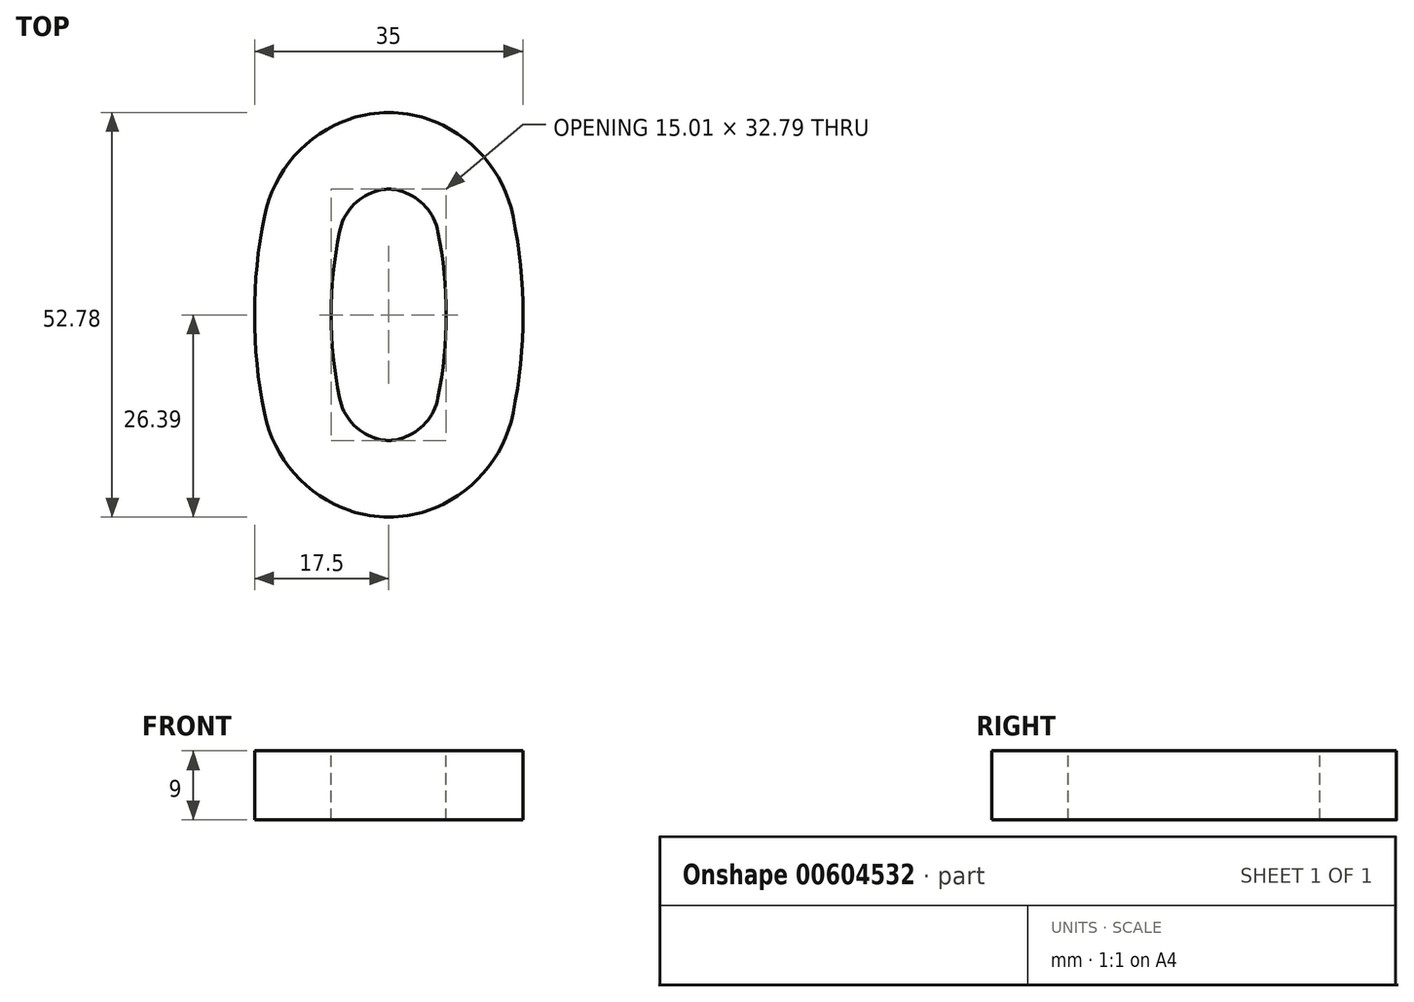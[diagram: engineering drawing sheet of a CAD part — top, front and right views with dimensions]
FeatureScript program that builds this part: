
annotation { "Feature Type Name" : "Feature", "Feature Type Description" : "" }
export const myFeature = defineFeature(function(context is Context, id is Id, definition is map)
    precondition{}
    {
        {
            var Q0;
            Q0=qCreatedBy(makeId("Top.planeOp"),FACE);
            var sketch = newSketch(context, id + "F0", { "sketchPlane" : qUnion([Q0])});
            skLineSegment(sketch, "E0.bottom", {"start": v(-15.38, -16.5) * mm, "end": v(15.38, -16.5) * mm, "construction": true});
            skLineSegment(sketch, "E0.top", {"start": v(-15.37, 16.5) * mm, "end": v(15.38, 16.5) * mm, "construction": true});
            skLineSegment(sketch, "E0.left", {"start": v(-15.38, -16.5) * mm, "end": v(-15.38, 16.5) * mm, "construction": true});
            skLineSegment(sketch, "E0.right", {"start": v(15.38, -16.5) * mm, "end": v(15.38, 16.5) * mm, "construction": true});
            skPoint(sketch, "E0.middle", {"position": v(0, 0) * mm});
            skLineSegment(sketch, "E1", {"start": v(0, 26.5) * mm, "end": v(0, 16.5) * mm, "construction": true});
            skPoint(sketch, "E1.endSnap0", {"position": v(0, -16.5) * mm});
            skLineSegment(sketch, "E2", {"start": v(-15.38, 0) * mm, "end": v(15.38, 0) * mm, "construction": true});
            skLineSegment(sketch, "E3.trimOffspring", {"start": v(0, -16.5) * mm, "end": v(0, -26.5) * mm});
            skLineSegment(sketch, "E4", {"start": v(0, 16.5) * mm, "end": v(0, -16.5) * mm, "construction": true});
            skArc(sketch, "E5", {"start": v(15.38, 16.5) * mm, "mid": v(9.06, 23.6) * mm, "end": v(0, 26.5) * mm});
            skArc(sketch, "E6", {"start": v(0, -26.5) * mm, "mid": v(9.06, -23.6) * mm, "end": v(15.38, -16.5) * mm});
            skArc(sketch, "E7", {"start": v(0, 26.5) * mm, "mid": v(-9.06, 23.6) * mm, "end": v(-15.37, 16.5) * mm});
            skArc(sketch, "E8", {"start": v(-15.38, -16.5) * mm, "mid": v(-9.06, -23.6) * mm, "end": v(0, -26.5) * mm});
            skArc(sketch, "E9", {"start": v(15.38, -16.5) * mm, "mid": v(17.5, 0) * mm, "end": v(15.38, 16.5) * mm});
            skArc(sketch, "E10", {"start": v(-15.38, 16.5) * mm, "mid": v(-17.5, 0) * mm, "end": v(-15.38, -16.5) * mm});
            skSolve(sketch);
        }
        {
            var Q0;
            Q0=makeQuery(id+"F0.imprint","IMPRINT",FACE,{"disambiguationData":[TD([[makeQuery(id+"F0.imprint","IMPRINT",EDGE,{"derivedFrom":sQuery(id+"F0.wireOp",EDGE,"E5")}),1.0]])]});
            extrude(context, id + "F1", {"entities" : qUnion([Q0]), "depth" : 9 * mm, "offsetDistance" : 25 * mm, "symmetric" : true});
        }
        {
            var Q0;
            Q0=makeQuery(id+"F1.opExtrude","SWEPT_EDGE",EDGE,{"disambiguationData":[OSD([sQuery(id+"F0.wireOp",EDGE,"E7"),sQuery(id+"F0.wireOp",EDGE,"E10")])]});
            var Q1;
            Q1=makeQuery(id+"F1.opExtrude","SWEPT_EDGE",EDGE,{"disambiguationData":[OSD([sQuery(id+"F0.wireOp",EDGE,"E8"),sQuery(id+"F0.wireOp",EDGE,"E10")])]});
            var Q2;
            Q2=makeQuery(id+"F1.opExtrude","SWEPT_EDGE",EDGE,{"disambiguationData":[OSD([sQuery(id+"F0.wireOp",EDGE,"E6"),sQuery(id+"F0.wireOp",EDGE,"E9")])]});
            var Q3;
            Q3=makeQuery(id+"F1.opExtrude","SWEPT_EDGE",EDGE,{"disambiguationData":[OSD([sQuery(id+"F0.wireOp",EDGE,"E5"),sQuery(id+"F0.wireOp",EDGE,"E9")])]});
            fillet(context, id + "F2", {"entities" : qUnion([Q0, Q1, Q2, Q3]), "radius" : 17 * mm, "tangentPropagation" : true, "allowEdgeOverflow" : false});
        }
        {
            var Q0;
            Q0=makeQuery(id+"F1.opExtrude","SWEPT_EDGE",EDGE,{"disambiguationData":[OSD([sQuery(id+"F0.wireOp",EDGE,"E5"),sQuery(id+"F0.wireOp",EDGE,"E7")])]});
            var Q1;
            Q1=makeQuery(id+"F1.opExtrude","SWEPT_EDGE",EDGE,{"disambiguationData":[OSD([sQuery(id+"F0.wireOp",EDGE,"E6"),sQuery(id+"F0.wireOp",EDGE,"E8")])]});
            fillet(context, id + "F3", {"entities" : qUnion([Q0, Q1]), "radius" : 15.6 * mm, "tangentPropagation" : true, "allowEdgeOverflow" : false});
        }
        {
            var Q0;
            Q0=makeQuery(id+"F1.opExtrude","CAP_FACE",FACE,{"disambiguationData":[OSD([sQuery(id+"F0.wireOp",EDGE,"E5"),sQuery(id+"F0.wireOp",EDGE,"E6"),sQuery(id+"F0.wireOp",EDGE,"E7"),sQuery(id+"F0.wireOp",EDGE,"E8"),sQuery(id+"F0.wireOp",EDGE,"E9"),sQuery(id+"F0.wireOp",EDGE,"E10")])],"isStart":false});
            var sketch = newSketch(context, id + "F4", { "sketchPlane" : qUnion([Q0])});
            skArc(sketch, "E11.0.0", {"start": v(-5, -25.57) * mm, "mid": v(-4.95, -25.59) * mm, "end": v(-4.9, -25.6) * mm});
            skArc(sketch, "E11.0.1", {"start": v(-4.9, -25.6) * mm, "mid": v(0, -26.4) * mm, "end": v(4.9, -25.6) * mm});
            skArc(sketch, "E11.0.2", {"start": v(4.9, -25.6) * mm, "mid": v(4.95, -25.59) * mm, "end": v(5, -25.57) * mm});
            skArc(sketch, "E11.0.3", {"start": v(5, -25.57) * mm, "mid": v(12.32, -20.7) * mm, "end": v(16.23, -12.82) * mm});
            skArc(sketch, "E11.0.4", {"start": v(16.23, -12.82) * mm, "mid": v(17.5, 0) * mm, "end": v(16.23, 12.82) * mm});
            skArc(sketch, "E11.0.5", {"start": v(16.23, 12.82) * mm, "mid": v(12.32, 20.7) * mm, "end": v(5, 25.57) * mm});
            skArc(sketch, "E11.0.6", {"start": v(5, 25.57) * mm, "mid": v(4.95, 25.59) * mm, "end": v(4.9, 25.6) * mm});
            skArc(sketch, "E11.0.7", {"start": v(4.9, 25.6) * mm, "mid": v(0, 26.4) * mm, "end": v(-4.9, 25.6) * mm});
            skArc(sketch, "E11.0.8", {"start": v(-4.9, 25.6) * mm, "mid": v(-4.95, 25.59) * mm, "end": v(-5, 25.57) * mm});
            skArc(sketch, "E11.0.9", {"start": v(-5, 25.57) * mm, "mid": v(-12.32, 20.7) * mm, "end": v(-16.23, 12.82) * mm});
            skArc(sketch, "E11.0.10", {"start": v(-16.23, 12.82) * mm, "mid": v(-17.5, 0) * mm, "end": v(-16.23, -12.82) * mm});
            skArc(sketch, "E11.0.11", {"start": v(-16.23, -12.82) * mm, "mid": v(-12.32, -20.7) * mm, "end": v(-5, -25.57) * mm});
            skArc(sketch, "E12.0", {"start": v(-6.42, -10.84) * mm, "mid": v(-4.81, -14.1) * mm, "end": v(-1.8, -16.1) * mm});
            skArc(sketch, "E12.1", {"start": v(6.42, -10.84) * mm, "mid": v(7.5, 0) * mm, "end": v(6.42, 10.84) * mm});
            skArc(sketch, "E12.2", {"start": v(1.8, -16.1) * mm, "mid": v(4.81, -14.1) * mm, "end": v(6.42, -10.84) * mm});
            skArc(sketch, "E12.3", {"start": v(1.76, -16.11) * mm, "mid": v(1.78, -16.1) * mm, "end": v(1.8, -16.1) * mm});
            skArc(sketch, "E12.4", {"start": v(-1.76, -16.11) * mm, "mid": v(0, -16.4) * mm, "end": v(1.76, -16.11) * mm});
            skArc(sketch, "E12.5", {"start": v(6.42, 10.84) * mm, "mid": v(4.81, 14.1) * mm, "end": v(1.8, 16.1) * mm});
            skArc(sketch, "E12.6", {"start": v(-1.8, -16.1) * mm, "mid": v(-1.78, -16.1) * mm, "end": v(-1.76, -16.11) * mm});
            skArc(sketch, "E12.7", {"start": v(1.8, 16.1) * mm, "mid": v(1.78, 16.1) * mm, "end": v(1.76, 16.11) * mm});
            skArc(sketch, "E12.8", {"start": v(1.76, 16.11) * mm, "mid": v(0, 16.4) * mm, "end": v(-1.76, 16.11) * mm});
            skArc(sketch, "E12.9", {"start": v(-1.76, 16.11) * mm, "mid": v(-1.78, 16.1) * mm, "end": v(-1.8, 16.1) * mm});
            skArc(sketch, "E12.10", {"start": v(-1.8, 16.1) * mm, "mid": v(-4.81, 14.1) * mm, "end": v(-6.42, 10.84) * mm});
            skArc(sketch, "E12.11", {"start": v(-6.42, 10.84) * mm, "mid": v(-7.5, 0) * mm, "end": v(-6.42, -10.84) * mm});
            skSolve(sketch);
        }
        {
            var Q0;
            Q0=makeQuery(id+"F4.imprint","IMPRINT",FACE,{"disambiguationData":[TD([[makeQuery(id+"F4.imprint","IMPRINT",EDGE,{"derivedFrom":sQuery(id+"F4.wireOp",EDGE,"E12.0")}),1.0]])]});
            var Q1;
            Q1=makeQuery(id+"F1.opExtrude","CAP_FACE",FACE,{"disambiguationData":[OSD([sQuery(id+"F0.wireOp",EDGE,"E5"),sQuery(id+"F0.wireOp",EDGE,"E6"),sQuery(id+"F0.wireOp",EDGE,"E7"),sQuery(id+"F0.wireOp",EDGE,"E8"),sQuery(id+"F0.wireOp",EDGE,"E9"),sQuery(id+"F0.wireOp",EDGE,"E10")])],"isStart":true});
            extrude(context, id + "F5", {"entities" : qUnion([Q0]), "operationType" : NewBodyOperationType.REMOVE, "endBound" : BoundingType.UP_TO_SURFACE, "oppositeDirection" : true, "depth" : 25 * mm, "endBoundEntityFace" : qUnion([Q1]), "offsetDistance" : 25 * mm});
        }
    });
